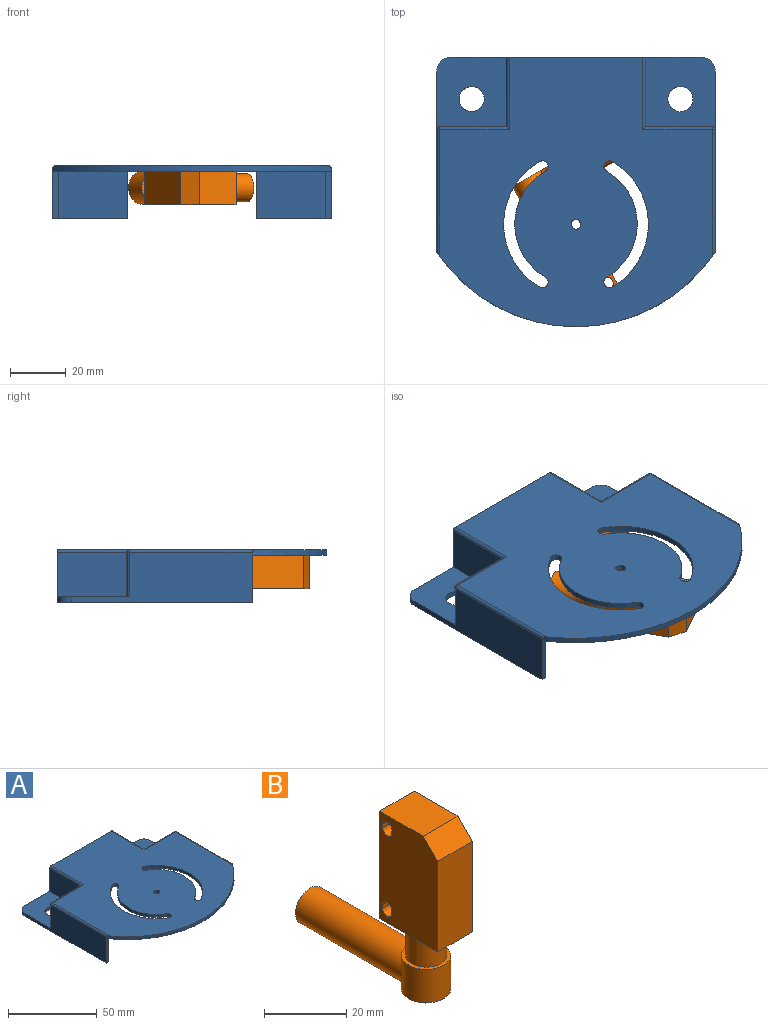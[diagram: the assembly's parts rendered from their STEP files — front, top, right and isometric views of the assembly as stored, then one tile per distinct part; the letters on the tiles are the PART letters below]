
ASSEMBLY  parts=2 mates=1
PART A: 45 faces, bbox 100x96.8x19 mm
  f0: plane 70x27mm, normal (0,0,-1), area 746mm2, adj f2,f6,f11,f13,f16,f28,f32,f44
  f1: plane 70x27mm, normal (0,0,-1), area 746mm2, adj f3,f7,f8,f11,f12,f29,f31,f43
  f2: plane 65x18mm, normal (-1,0,0), area 834mm2, adj f0,f14,f30,f32,f38,f39,f44
  f3: plane 65x18mm, normal (1,0,0), area 834mm2, adj f1,f9,f30,f31,f33,f34,f43
  f4: plane 98x96.83mm, normal (0,0,1), area 7009.7mm2, adj f11,f17,f18,f19,f20,f21,f22,f23
  f5: plane 100x96.83mm, normal (0,0,-1), area 6821.2mm2, adj f6,f7,f8,f11,f16,f17,f18,f19
  f6: plane 43x17mm, normal (1,0,0), area 731mm2, adj f0,f5,f16,f32
  f7: plane 43x17mm, normal (-1,0,0), area 731mm2, adj f1,f5,f8,f31
  f8: plane 25x17mm, normal (0,-1,0), area 425mm2, adj f1,f5,f7,f29
  f9: plane 26x25mm, normal (0,0,1), area 556.2mm2, adj f3,f11,f12,f15,f27,f33,f43
  f10: plane 24x16mm, normal (0,1,0), area 384mm2, adj f14,f26,f39,f41
  f11: plane 90x19mm, normal (0,1,0), area 247.6mm2, adj f0,f1,f4,f5,f9,f14,f26,f27
  f12: cylinder r=4.5mm len=9mm, axis (0,0,1), area 56.5mm2, adj f1,f9
  f13: cylinder r=4.5mm len=9mm, axis (0,0,1), area 56.5mm2, adj f0,f14
  f14: plane 26x25mm, normal (0,0,1), area 556.2mm2, adj f2,f10,f11,f13,f26,f39,f44
  f15: plane 24x16mm, normal (0,1,0), area 384mm2, adj f9,f27,f33,f37
  f16: plane 25x17mm, normal (0,-1,0), area 425mm2, adj f0,f5,f6,f28
  f17: cylinder r=2mm len=3.73mm, axis (0,0,1), area 12.6mm2, adj f4,f5,f18,f20
  f18: cylinder r=26mm len=45.03mm, axis (0,0,1), area 108.9mm2, adj f4,f5,f17,f19
  f19: cylinder r=2mm len=3.73mm, axis (0,0,1), area 12.6mm2, adj f4,f5,f18,f20
  f20: cylinder r=22mm len=38.11mm, axis (0,0,1), area 92.2mm2, adj f4,f5,f17,f19
  f21: cylinder r=1.75mm len=3.5mm, axis (0,0,1), area 22mm2, adj f4,f5
  f22: cylinder r=26mm len=45.03mm, axis (0,0,1), area 108.9mm2, adj f4,f5,f23,f25
  f23: cylinder r=2mm len=3.73mm, axis (0,0,1), area 12.6mm2, adj f4,f5,f22,f24
  f24: cylinder r=22mm len=38.11mm, axis (0,0,1), area 92.2mm2, adj f4,f5,f23,f25
  f25: cylinder r=2mm len=3.73mm, axis (0,0,1), area 12.6mm2, adj f4,f5,f22,f24
  f26: plane 25x16mm, normal (-1,0,0), area 400mm2, adj f10,f11,f14,f42
  f27: plane 25x16mm, normal (1,0,0), area 400mm2, adj f9,f11,f15,f35
  f28: plane 27x17mm, normal (1,0,0), area 459mm2, adj f0,f5,f11,f16
  f29: plane 27x17mm, normal (-1,0,0), area 459mm2, adj f1,f5,f8,f11
  f30: cylinder r=60mm len=100mm, axis (0,0,1), area 235.7mm2, adj f2,f3,f4,f5,f34,f38
  f31: plane 17x2mm, normal (0,-1,0), area 34mm2, adj f1,f3,f5,f7
  f32: plane 17x2mm, normal (0,-1,0), area 34mm2, adj f0,f2,f5,f6
  f33: cylinder r=1mm len=16mm, axis (0,0,-1), area 25.1mm2, adj f3,f9,f15,f36
  f34: cylinder r=1mm len=45.46mm, axis (0,-1,0), area 70mm2, adj f3,f4,f30,f36
  f35: cylinder r=1mm len=26mm, axis (0,-1,0), area 39.8mm2, adj f4,f11,f27,f37
  f36: sphere r=1mm, area 1.6mm2, adj f33,f34,f37
  f37: cylinder r=1mm len=25mm, axis (1,0,0), area 38.3mm2, adj f4,f15,f35,f36
  f38: cylinder r=1mm len=45.46mm, axis (0,1,0), area 70mm2, adj f2,f4,f30,f40
  f39: cylinder r=1mm len=16mm, axis (0,0,-1), area 25.1mm2, adj f2,f10,f14,f40
  f40: sphere r=1mm, area 1.6mm2, adj f38,f39,f41
  f41: cylinder r=1mm len=25mm, axis (1,0,0), area 38.3mm2, adj f4,f10,f40,f42
  f42: cylinder r=1mm len=26mm, axis (0,1,0), area 39.8mm2, adj f4,f11,f26,f41
  f43: cylinder r=5mm len=5mm, axis (0,0,-1), area 15.7mm2, adj f1,f3,f9,f11
  f44: cylinder r=5mm len=5mm, axis (0,0,1), area 15.7mm2, adj f0,f2,f11,f14
PART B: 21 faces, bbox 12x50x51 mm
  f0: plane 32x20mm, normal (1,0,0), area 605mm2, adj f2,f3,f4,f5,f6,f11,f12,f13
  f1: plane 32x20mm, normal (-1,0,0), area 605mm2, adj f2,f3,f4,f5,f6,f11,f12,f13
  f2: plane 20x12mm, normal (0,0,-1), area 161.5mm2, adj f0,f1,f3,f5,f7
  f3: plane 32x12mm, normal (0,1,0), area 384mm2, adj f0,f1,f2,f4
  f4: plane 15x12mm, normal (0,0,1), area 180mm2, adj f0,f1,f3,f6
  f5: plane 27x12mm, normal (0,-1,0), area 324mm2, adj f0,f1,f2,f6
  f6: plane 12x5mm, normal (0,-0.71,0.71), area 84.9mm2, adj f0,f1,f4,f5
  f7: cylinder r=5mm len=10mm, axis (0,0,1), area 282.7mm2, adj f2,f10
  f8: cylinder r=6mm len=12mm, axis (0,0,1), area 288.7mm2, adj f9,f10,f19
  f9: plane 12x12mm, normal (0,0,-1), area 113.1mm2, adj f8
  f10: plane 12x12mm, normal (0,0,1), area 34.6mm2, adj f7,f8
  f11: cylinder r=1.6mm len=12mm, axis (1,0,0), area 60.3mm2, adj f0,f1,f12,f14
  f12: plane 12x1mm, normal (0,1,0), area 12mm2, adj f0,f1,f11,f13
  f13: cylinder r=1.6mm len=12mm, axis (1,0,0), area 60.3mm2, adj f0,f1,f12,f14
  f14: plane 12x1mm, normal (0,-1,0), area 12mm2, adj f0,f1,f11,f13
  f15: cylinder r=1.6mm len=12mm, axis (1,0,0), area 60.3mm2, adj f0,f1,f16,f18
  f16: plane 12x1mm, normal (0,-1,0), area 12mm2, adj f0,f1,f15,f17
  f17: cylinder r=1.6mm len=12mm, axis (1,0,0), area 60.3mm2, adj f0,f1,f16,f18
  f18: plane 12x1mm, normal (0,1,0), area 12mm2, adj f0,f1,f15,f17
  f19: cylinder r=5mm len=36.68mm, axis (0,-1,0), area 1107.2mm2, adj f8,f20
  f20: plane 10x10mm, normal (0,1,0), area 78.5mm2, adj f19
PLACE A at identity fixed
PLACE B rot(axis=(0.45,0.77,-0.45),105deg) t=(-0.68,-24.08,11)mm
MATE revolute B.f1 <-> A.f20  axis (0,0,1) through (0,-10,17)mm
